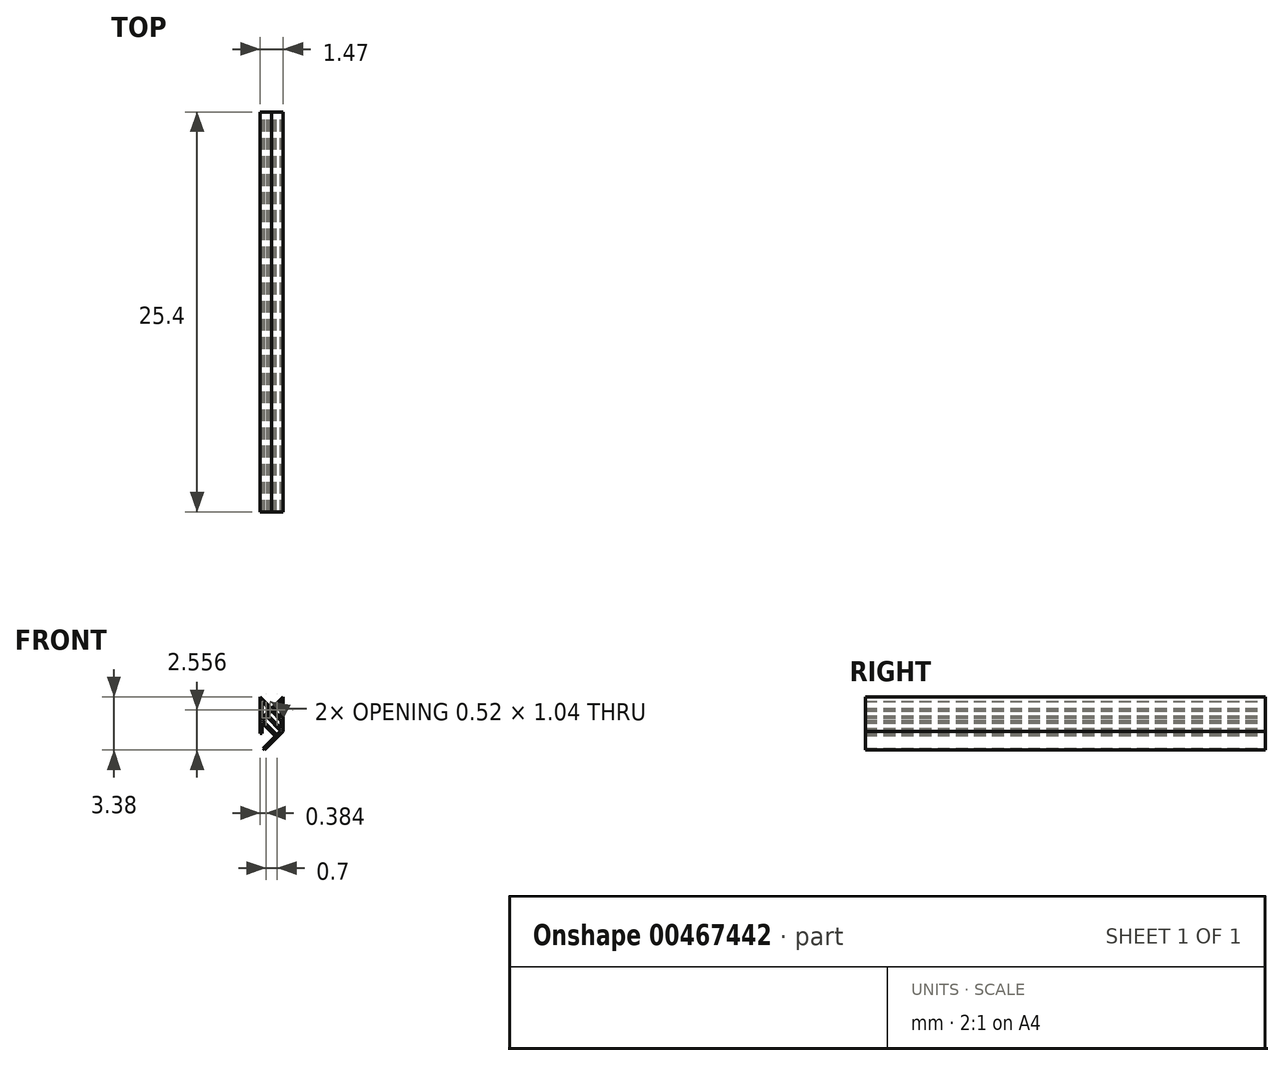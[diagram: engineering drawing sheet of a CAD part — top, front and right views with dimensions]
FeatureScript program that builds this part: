
annotation { "Feature Type Name" : "Feature", "Feature Type Description" : "" }
export const myFeature = defineFeature(function(context is Context, id is Id, definition is map)
    precondition{}
    {
        {
            var Q0;
            Q0=qCreatedBy(makeId("Front.planeOp"),FACE);
            var sketch = newSketch(context, id + "F0", { "sketchPlane" : qUnion([Q0])});
            skLineSegment(sketch, "E0.0", {"start": v(1.28, -0.15) * mm, "end": v(1.28, -1.2) * mm});
            skLineSegment(sketch, "E1.0", {"start": v(1.41, 0.15) * mm, "end": v(1.41, -2.05) * mm});
            skLineSegment(sketch, "E2.0", {"start": v(1.41, 0.15) * mm, "end": v(0.67, -0.58) * mm});
            skLineSegment(sketch, "E3.0", {"start": v(1.28, -0.15) * mm, "end": v(0.76, -0.67) * mm});
            skLineSegment(sketch, "E4.0", {"start": v(0.06, -0.15) * mm, "end": v(0.58, -0.67) * mm});
            skLineSegment(sketch, "E5.0", {"start": v(-0.06, 0.15) * mm, "end": v(0.67, -0.58) * mm});
            skLineSegment(sketch, "E6.0", {"start": v(-0.06, 0.15) * mm, "end": v(-0.06, -2.17) * mm});
            skLineSegment(sketch, "E7.0", {"start": v(0.06, -0.15) * mm, "end": v(0.06, -1.2) * mm});
            skLineSegment(sketch, "E8.trimOffspring", {"start": v(0.58, -0.67) * mm, "end": v(0.06, -1.2) * mm});
            skLineSegment(sketch, "E9.trimOffspring", {"start": v(0.67, -0.76) * mm, "end": v(0.09, -1.35) * mm});
            skLineSegment(sketch, "E10.trimOffspring", {"start": v(0.67, -0.76) * mm, "end": v(1.28, -1.37) * mm});
            skLineSegment(sketch, "E11.trimOffspring", {"start": v(0.76, -0.67) * mm, "end": v(1.28, -1.2) * mm});
            skLineSegment(sketch, "E12.trimOffspring", {"start": v(0.06, -1.5) * mm, "end": v(0.06, -2.17) * mm});
            skLineSegment(sketch, "E13.trimOffspring", {"start": v(1.28, -1.37) * mm, "end": v(1.28, -1.87) * mm});
            skLineSegment(sketch, "E14.0", {"start": v(0.47, -1.06) * mm, "end": v(1.28, -1.87) * mm});
            skLineSegment(sketch, "E15.0", {"start": v(0.38, -1.14) * mm, "end": v(1.26, -2.02) * mm});
            skLineSegment(sketch, "E16.0", {"start": v(1.26, -2.02) * mm, "end": v(0.13, -3.14) * mm});
            skLineSegment(sketch, "E17", {"start": v(0.38, -1.14) * mm, "end": v(0.47, -1.06) * mm});
            skLineSegment(sketch, "E18", {"start": v(0.13, -3.14) * mm, "end": v(0.22, -3.23) * mm});
            skLineSegment(sketch, "E19.0", {"start": v(0.06, -1.5) * mm, "end": v(0.88, -2.31) * mm});
            skLineSegment(sketch, "E20.0", {"start": v(0.09, -1.35) * mm, "end": v(0.97, -2.22) * mm});
            skLineSegment(sketch, "E21", {"start": v(0.88, -2.31) * mm, "end": v(0.97, -2.22) * mm});
            skLineSegment(sketch, "E22", {"start": v(0.06, -2.17) * mm, "end": v(-0.06, -2.17) * mm});
            skLineSegment(sketch, "E23", {"start": v(1.41, -2.05) * mm, "end": v(0.22, -3.23) * mm});
            skSolve(sketch);
        }
        {
            var Q0;
            Q0 = qSketchRegion(id + "F0", true);
            extrude(context, id + "F1", {"entities" : qUnion([Q0]), "depth" : 25.4 * mm});
        }
    });
